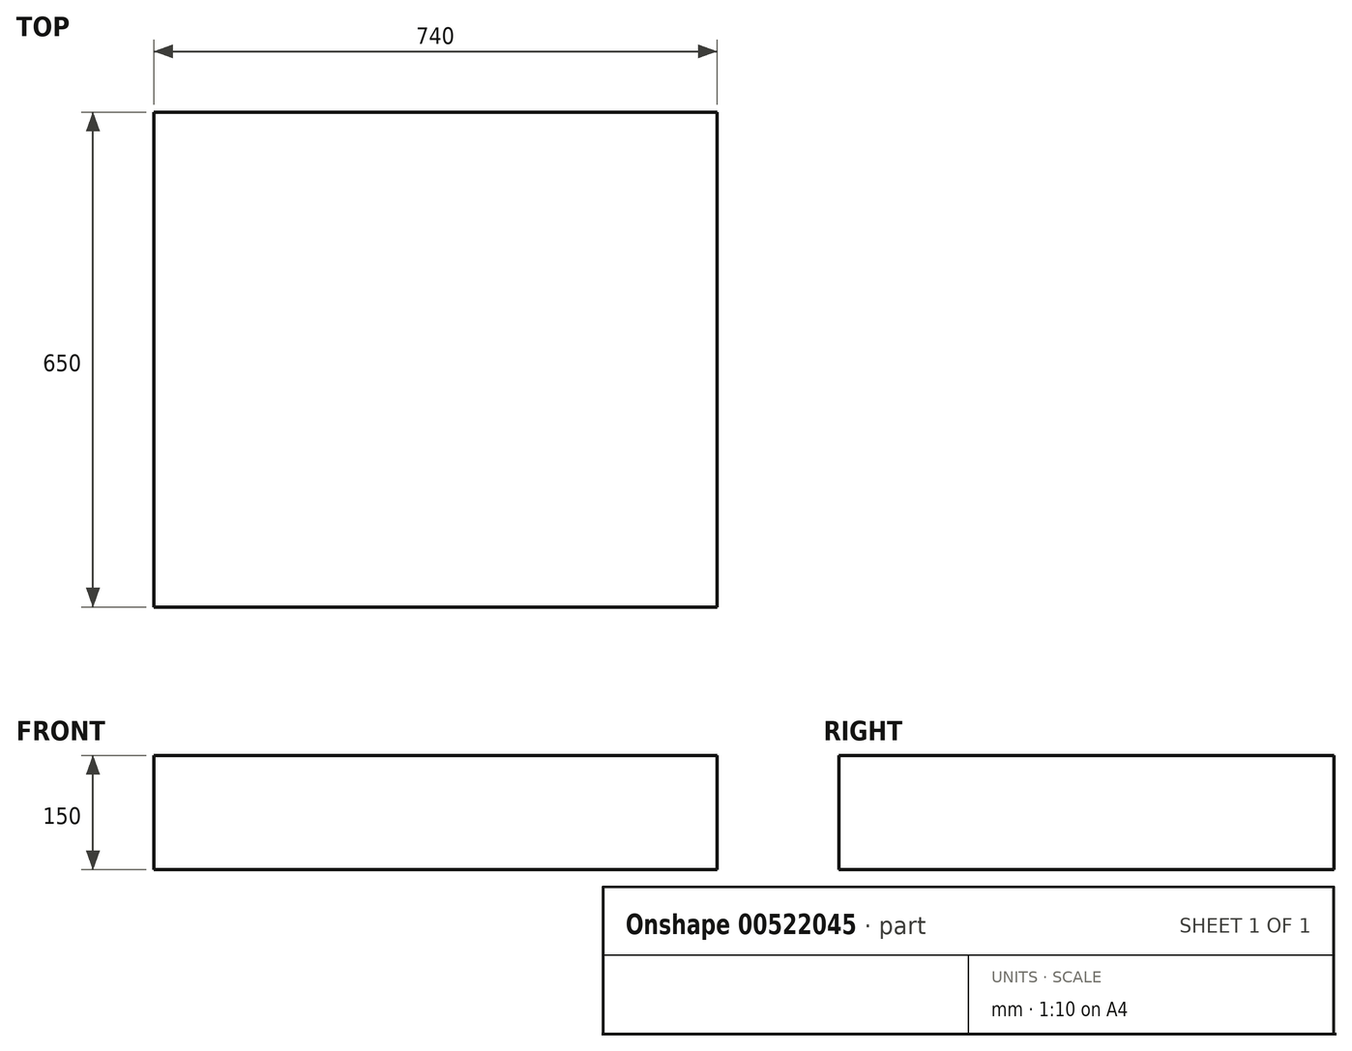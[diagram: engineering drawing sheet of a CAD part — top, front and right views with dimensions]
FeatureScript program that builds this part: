
annotation { "Feature Type Name" : "Feature", "Feature Type Description" : "" }
export const myFeature = defineFeature(function(context is Context, id is Id, definition is map)
    precondition{}
    {
        {
            var Q0;
            Q0=qCreatedBy(makeId("Top.planeOp"),FACE);
            var sketch = newSketch(context, id + "F0", { "sketchPlane" : qUnion([Q0])});
            skLineSegment(sketch, "E0.bottom", {"start": v(0, 0) * mm, "end": v(-740, 0) * mm});
            skLineSegment(sketch, "E0.top", {"start": v(0, 650) * mm, "end": v(-740, 650) * mm});
            skLineSegment(sketch, "E0.left", {"start": v(0, 0) * mm, "end": v(0, 650) * mm});
            skLineSegment(sketch, "E0.right", {"start": v(-740, 0) * mm, "end": v(-740, 650) * mm});
            skSolve(sketch);
        }
        {
            var Q0;
            Q0=makeQuery(id+"F0.imprint","IMPRINT",FACE,{"disambiguationData":[TD([[makeQuery(id+"F0.imprint","IMPRINT",EDGE,{"derivedFrom":sQuery(id+"F0.wireOp",EDGE,"E0.bottom")}),-1.0]])]});
            extrude(context, id + "F1", {"entities" : qUnion([Q0]), "depth" : 150 * mm, "offsetDistance" : 25 * mm});
        }
    });
